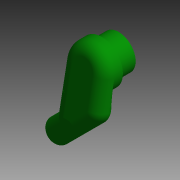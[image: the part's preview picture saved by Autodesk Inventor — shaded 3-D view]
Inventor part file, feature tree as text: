
AUTODESK INVENTOR PART (.ipt)
format: ipt  version: 2015 (Build 190159000, 159)  size: 334,336 bytes
history: native  units: mm (DEFAULTED — no unit token found)
features: sketch x10, other x4
ambient origin geometry x8: Origin, YZ Plane, XZ Plane, XY Plane, X Axis, Y Axis, Z Axis, Center Point
bodies: Solid1 (feature_tree), Solid2 (feature_tree)
feature tree (14):
  other  "ARM LHS.ipt"
  other  "Solid4::ARM LHS.ipt"
  other  "Solid5::ARM LHS.ipt"
  sketch  "Sketch1"  dims[d0=10.0mm]
  sketch  "Sketch2"
  sketch  "Sketch3"
  sketch  "Sketch4"
  sketch  "Sketch6"
  sketch  "Sketch10"
  sketch  "Sketch13"
  sketch  "Sketch14"
  sketch  "Sketch15"
  sketch  "Sketch16"
  other  "TaggingFeature1"
